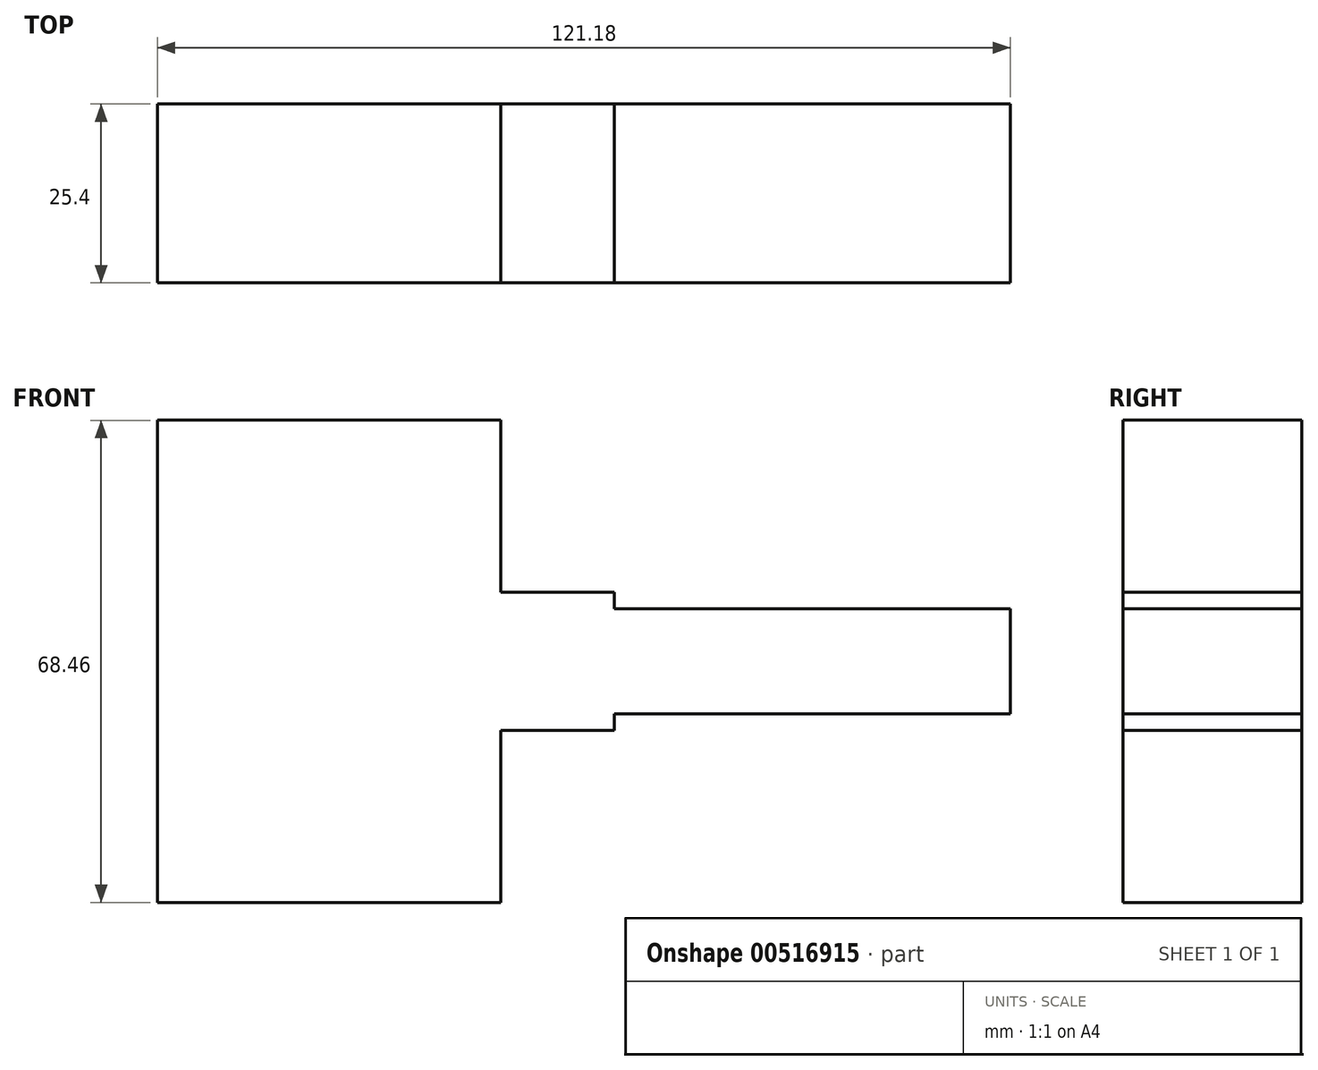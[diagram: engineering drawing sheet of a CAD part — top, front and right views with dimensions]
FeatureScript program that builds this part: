
annotation { "Feature Type Name" : "Feature", "Feature Type Description" : "" }
export const myFeature = defineFeature(function(context is Context, id is Id, definition is map)
    precondition{}
    {
        {
            var Q0;
            Q0=qCreatedBy(makeId("Front.planeOp"),FACE);
            var sketch = newSketch(context, id + "F0", { "sketchPlane" : qUnion([Q0])});
            skLineSegment(sketch, "E0.bottom", {"start": v(-24.4, 34.23) * mm, "end": v(24.4, 34.23) * mm});
            skLineSegment(sketch, "E0.top", {"start": v(-24.4, -34.23) * mm, "end": v(24.4, -34.23) * mm});
            skLineSegment(sketch, "E0.left", {"start": v(-24.4, 34.23) * mm, "end": v(-24.4, -34.23) * mm});
            skLineSegment(sketch, "E0.right", {"start": v(24.4, 34.23) * mm, "end": v(24.4, -34.23) * mm});
            skPoint(sketch, "E0.middle", {"position": v(0, 0) * mm});
            skPoint(sketch, "E1", {"position": v(24.4, 0) * mm});
            skLineSegment(sketch, "E2.bottom", {"start": v(40.53, 9.84) * mm, "end": v(8.26, 9.84) * mm});
            skLineSegment(sketch, "E2.top", {"start": v(40.53, -9.84) * mm, "end": v(8.26, -9.84) * mm});
            skLineSegment(sketch, "E2.left", {"start": v(40.53, 9.84) * mm, "end": v(40.53, -9.84) * mm});
            skLineSegment(sketch, "E2.right", {"start": v(8.26, 9.84) * mm, "end": v(8.26, -9.84) * mm});
            skPoint(sketch, "E3", {"position": v(40.53, 0) * mm});
            skLineSegment(sketch, "E4.bottom", {"start": v(96.8, 7.48) * mm, "end": v(-15.74, 7.48) * mm});
            skLineSegment(sketch, "E4.top", {"start": v(96.8, -7.48) * mm, "end": v(-15.74, -7.48) * mm});
            skLineSegment(sketch, "E4.left", {"start": v(96.8, 7.48) * mm, "end": v(96.8, -7.48) * mm});
            skLineSegment(sketch, "E4.right", {"start": v(-15.74, 7.48) * mm, "end": v(-15.74, -7.48) * mm});
            skSolve(sketch);
        }
        {
            var Q0;
            {var subQ14=sQuery(id+"F0.wireOp",EDGE,"E0.bottom");Q0=makeQuery(id+"F0.imprint","IMPRINT",FACE,{"disambiguationData":[TD([[makeQuery(id+"F0.imprint","IMPRINT",EDGE,{"derivedFrom":subQ14}),-1.0]])]});}
            var sketch = newSketch(context, id + "F1", { "sketchPlane" : qUnion([Q0])});
            skSolve(sketch);
        }
        {
            var Q0;
            Q0 = qSketchRegion(id + "F1", true);
            var Q1;
            {var subQ5=sQuery(id+"F0.wireOp",EDGE,"E4.right");Q1=makeQuery(id+"F0.imprint","IMPRINT",FACE,{"disambiguationData":[TD([[makeQuery(id+"F0.imprint","IMPRINT",EDGE,{"derivedFrom":subQ5}),1.0]])]});}
            var Q2;
            {var subQ14=sQuery(id+"F0.wireOp",EDGE,"E0.bottom");Q2=makeQuery(id+"F0.imprint","IMPRINT",FACE,{"disambiguationData":[TD([[makeQuery(id+"F0.imprint","IMPRINT",EDGE,{"derivedFrom":subQ14}),-1.0]])]});}
            var Q3;
            {var subQ0=sQuery(id+"F0.wireOp",EDGE,"E4.bottom");var subQ1=sQuery(id+"F0.wireOp",EDGE,"E0.right");var subQ2=makeQuery(id+"F0.imprint","INTERSECT",VERTEX,{"derivedFrom":[subQ1,subQ0]});Q3=makeQuery(id+"F0.imprint","IMPRINT",FACE,{"disambiguationData":[TD([[makeQuery(id+"F0.imprint","IMPRINT",EDGE,{"disambiguationData":[TD([[subQ2,-1.0]])],"derivedFrom":subQ1}),1.0]])]});}
            var Q4;
            {var subQ0=sQuery(id+"F0.wireOp",EDGE,"E4.bottom");var subQ1=sQuery(id+"F0.wireOp",EDGE,"E0.right");var subQ2=makeQuery(id+"F0.imprint","INTERSECT",VERTEX,{"derivedFrom":[subQ1,subQ0]});Q4=makeQuery(id+"F0.imprint","IMPRINT",FACE,{"disambiguationData":[TD([[makeQuery(id+"F0.imprint","IMPRINT",EDGE,{"disambiguationData":[TD([[subQ2,-1.0]])],"derivedFrom":subQ1}),-1.0]])]});}
            var Q5;
            {var subQ0=sQuery(id+"F0.wireOp",EDGE,"E2.bottom");var subQ1=sQuery(id+"F0.wireOp",EDGE,"E0.right");var subQ2=makeQuery(id+"F0.imprint","INTERSECT",VERTEX,{"derivedFrom":[subQ1,subQ0]});Q5=makeQuery(id+"F0.imprint","IMPRINT",FACE,{"disambiguationData":[TD([[makeQuery(id+"F0.imprint","IMPRINT",EDGE,{"disambiguationData":[TD([[subQ2,-1.0]])],"derivedFrom":subQ1}),-1.0]])]});}
            var Q6;
            {var subQ0=sQuery(id+"F0.wireOp",EDGE,"E2.bottom");var subQ1=sQuery(id+"F0.wireOp",EDGE,"E0.right");var subQ2=makeQuery(id+"F0.imprint","INTERSECT",VERTEX,{"derivedFrom":[subQ1,subQ0]});Q6=makeQuery(id+"F0.imprint","IMPRINT",FACE,{"disambiguationData":[TD([[makeQuery(id+"F0.imprint","IMPRINT",EDGE,{"disambiguationData":[TD([[subQ2,-1.0]])],"derivedFrom":subQ1}),1.0]])]});}
            var Q7;
            {var subQ0=sQuery(id+"F0.wireOp",EDGE,"E2.top");var subQ1=sQuery(id+"F0.wireOp",EDGE,"E0.right");var subQ2=makeQuery(id+"F0.imprint","INTERSECT",VERTEX,{"derivedFrom":[subQ1,subQ0]});Q7=makeQuery(id+"F0.imprint","IMPRINT",FACE,{"disambiguationData":[TD([[makeQuery(id+"F0.imprint","IMPRINT",EDGE,{"disambiguationData":[TD([[subQ2,1.0]])],"derivedFrom":subQ1}),-1.0]])]});}
            var Q8;
            {var subQ0=sQuery(id+"F0.wireOp",EDGE,"E2.top");var subQ1=sQuery(id+"F0.wireOp",EDGE,"E0.right");var subQ2=makeQuery(id+"F0.imprint","INTERSECT",VERTEX,{"derivedFrom":[subQ1,subQ0]});Q8=makeQuery(id+"F0.imprint","IMPRINT",FACE,{"disambiguationData":[TD([[makeQuery(id+"F0.imprint","IMPRINT",EDGE,{"disambiguationData":[TD([[subQ2,1.0]])],"derivedFrom":subQ1}),1.0]])]});}
            var Q9;
            {var subQ5=sQuery(id+"F0.wireOp",EDGE,"E4.left");Q9=makeQuery(id+"F0.imprint","IMPRINT",FACE,{"disambiguationData":[TD([[makeQuery(id+"F0.imprint","IMPRINT",EDGE,{"derivedFrom":subQ5}),-1.0]])]});}
            extrude(context, id + "F2", {"entities" : qUnion([Q0, Q1, Q2, Q3, Q4, Q5, Q6, Q7, Q8, Q9]), "endBound" : BoundingType.SYMMETRIC, "depth" : 25.4 * mm, "offsetDistance" : 25.4 * mm});
        }
        {
            var Q0;
            Q0=qCreatedBy(makeId("Front.planeOp"),FACE);
            var sketch = newSketch(context, id + "F3", { "sketchPlane" : qUnion([Q0])});
            skCircle(sketch, "E5", {"center": v(-10.17, 26.64) * mm, "radius": 6.37 * mm});
            skSolve(sketch);
        }
        {
            var Q0;
            Q0=makeQuery(id+"F2.opExtrude","CAP_FACE",FACE,{"disambiguationData":[OSD([sQuery(id+"F0.wireOp",EDGE,"E0.bottom"),sQuery(id+"F0.wireOp",EDGE,"E0.top"),sQuery(id+"F0.wireOp",EDGE,"E0.left"),sQuery(id+"F0.wireOp",EDGE,"E0.right"),sQuery(id+"F0.wireOp",EDGE,"E2.bottom"),sQuery(id+"F0.wireOp",EDGE,"E2.top"),sQuery(id+"F0.wireOp",EDGE,"E2.left"),sQuery(id+"F0.wireOp",EDGE,"E4.bottom"),sQuery(id+"F0.wireOp",EDGE,"E4.top"),sQuery(id+"F0.wireOp",EDGE,"E4.left")])],"isStart":true});
            extrude(context, id + "F4", {"entities" : qUnion([Q0]), "operationType" : NewBodyOperationType.ADD, "oppositeDirection" : true, "depth" : 25.4 * mm, "offsetDistance" : 25.4 * mm});
        }
        {
            var Q0;
            Q0=sQuery(id+"F3.wireOp",EDGE,"E5");
            extrude(context, id + "F5", {"bodyType" : ToolBodyType.SURFACE, "surfaceEntities" : qUnion([Q0]), "oppositeDirection" : true, "depth" : 25.4 * mm, "offsetDistance" : 25.4 * mm});
        }
        {
            var Q0;
            Q0=makeQuery(id+"F5.opExtrude","SWEPT_BODY",BODY,{"disambiguationData":[OSD([sQuery(id+"F3.wireOp",EDGE,"E5")])]});
            deleteBodies(context, id + "F6", {"entities" : qUnion([Q0])});
        }
    });
